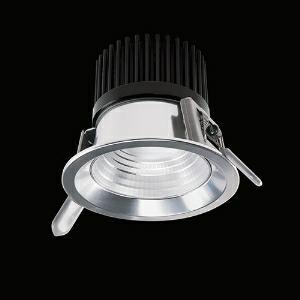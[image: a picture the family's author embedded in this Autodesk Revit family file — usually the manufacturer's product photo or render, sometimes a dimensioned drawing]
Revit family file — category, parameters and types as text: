
# Revit family: spectral_myral_myral_4500-840-m
name_source: partatom
category: Lighting Fixtures
revit_build: Autodesk Revit 2016 (Build: 20150220_1215(x64)
units: mm (PartAtom-declared; Revit-internal decimal feet)

## family parameters
Cut with Voids When Loaded = No
Host = Face
Light Source = No
Part Type = Normal
Room Calculation Point = No
Round Connector Dimension = Use Diameter
Shared = No

## types (1)
- SPECTRAL MYRAL (1 x )
    Apparent Load = 0 VA
    Approval mark = CE
    CIE Flux Codes = 82 99 100 100 100
    Control Gear = Electronic transformer
    Default Elevation = 1800 mm
    Description = SPG0320183
MYRAL recessed spot

Design:
    Height = 0 mm  [stored 0 ft]
    Lamp = 1 x
    Lamp count = 1
    Length = 120 mm
    Luminous efficacy = 0 lm/W
    Manufacturer = Ridi
    ModVariant = No
    Model = MYRAL 4500-840-M
    Mounting Place = Ceiling
    Mounting Type = Recessed
    Number of Poles = 1
    OnlyDefault = Yes
    Power Factor = 1
    Product Name = SPECTRAL MYRAL
    Product group = Downlight recessed
    ProductGroupID = 400
    Protection Class = Protection class
    Protection Degree = IP 20
    RlxData = <blob elided: 38677 chars, md5=602054c7>
    Socket = socket
    Standby Power = 0 W
    System Light Flux = 0 lm
    System Power = 0 W
    Type Image = myral_04.jpg
    URL = http://reluxnet.relux.com
    VarID = ---
    Voltage = 0 V
    Weight = 0.00 kg
    Width = 0 mm  [stored 0 ft]

note: [stored X ft] marks values corroborated as IEEE doubles in the binary element streams (Revit-internal decimal feet)

## geometry (parser evidence)
native form markers: Sweep x11
no freeform markers — native parametric forms only
